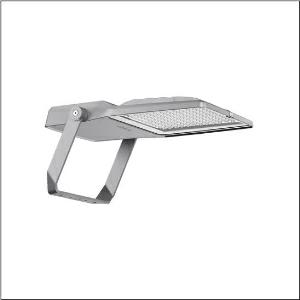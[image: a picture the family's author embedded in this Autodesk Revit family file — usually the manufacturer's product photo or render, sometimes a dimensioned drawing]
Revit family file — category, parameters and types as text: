
# Revit family: floodlight_fl_21_iq_midi___rs12_5xa7782e5b1a_e229
name_source: partatom
category: Lighting Fixtures
units: mm (PartAtom-declared; Revit-internal decimal feet)

## family parameters
Cut with Voids When Loaded = No
Host = Face
Light Source = No
Part Type = Normal
Room Calculation Point = No
Round Connector Dimension = Use Diameter
Shared = No

## types (1)
- --- (1 x LED, 24940 lm, 208.1 W, 4000K)
    Apparent Load = 208 VA
    CIE Flux Codes = 79 92 99 100 100
    Color Rendering = 80
    Color Temperature = 4000K
    Default Elevation = 1800 mm
    Description = Floodlight FL 21 iQ midi, floodlight, primary light control with lens, of PMMA, primary optical cover: protective disc, of toughened safety glass, transparent, light distribution: RS12, light emission: direct distribution, installation type: surface-mounted, LED, High Power LED, rated luminous flux: 24.940lm, luminous efficacy: 120lm/W, light colour: 840, colour temperature: 4000K, control gear: ECG iQ, control: optimised constant luminous flux control (CLO 2.0), Desk-Remote (wireless, voltage-free reading and setting of iQ features in the workshop via application-optimized NFC function/RFID function), Smart-Wire, Night-Set, Temp-Guard, Street-Remote, Auto-Match, with terminal, 6-pole, mains connection: 220..240V, AC, 50/60Hz, start of lifetime: 208W, end of service life: 227W, reduction: 90W, luminaire housing, of diecast aluminium, powder-coated, Siteco® metallic grey (DB 702S), corrosivity category C5 mid according to DIN EN ISO 12944, sealing non-destructively replaceable, mounting bracket, of steel, galvanised, powder-coated, Siteco® metallic grey (DB 702S), protection rating (complete): IP66, insulation class (complete): insulation class II (safety insulation), certification: CE, protection symbol: D, impact resistance: IK08, permissible operating ambient temperature: -40..+40°C, permissible operating ambient temperature for outdoor applications: -40..+50°C, standard: DIN EN 12944, LABS conformity tested according to VDMA 24364:2018-05, packaging unit: 1 piece

Light Distribution: RS12
    Height = 76 mm
    Lamp = 1 x LED
    Lamp Light Flux = 24940 lm
    Lamp Power = 208.1 W
    Lamp count = 1
    Length = 657 mm
    Luminous efficacy = 120 lm/W
    Manufacturer = Siteco
    ModVariant = No
    Model = 5XA7782E5B1A
    Number of Poles = 1
    OnlyDefault = Yes
    Power Factor = 1
    Product Name = Floodlight FL 21 iQ midi | RS12
    Product group = floodlight | pylon annexe
    ProductGroupID = 6200
    Protection Class = Protection class II
    Protection Degree = IP 66
    RLX_Detail_Level = 1
    RLX_Emergency_Light_Flux = 0 lm
    RLX_Emergency_Type = 0
    RLX_Emergency_Type_DB = No
    RlxData = <blob elided: 141381 chars, md5=2f02c431>
    Socket = socket
    Standby Power = 0 W
    System Light Flux = 24940 lm
    System Power = 208 W
    Type Comments = factory setting: luminous flux: 100 % | dim-lin: 254 | 710 mA
    Type Image = l_1006876.jpg
    URL = http://relux.com
    VarID = @adj_037831
    Voltage = 0 V
    Weight = 0.00 kg
    Width = 442 mm

## geometry (parser evidence)
native form markers: Blend x4, Sweep x13
no freeform markers — native parametric forms only
